# Revit family: Tables-Meeting-Teknion-BC_MRLB_Rectangular_Meeting_Table_Blade_Legs-R2019
name_source: partatom
category: Furniture
units: mm (PartAtom-declared; Revit-internal decimal feet)

## family parameters
Always vertical = Yes
Cut with Voids When Loaded = No
OmniClass Number = 23.40.20.00
OmniClass Title = General Furniture and Specialties
Room Calculation Point = No
Shared = Yes
Work Plane-Based = No

## types (6) — shared parameters
Assembly Code = E2020200
Manufacturer = Teknion
Manufacturer Fax = 416.661.4586
Part Number = BC_MRLB
Product Documentation Link = https://www.teknion.com
Product Line = Expansion Casegoods
Product Page URL = https://www.teknion.com
Series = Expansion Casegoods
Sustainability Data = https://www.teknion.com
URL = www.teknion.com
Unit Weight URL = http://www.teknion.com
Warranty = http://www.teknion.com

## per-type parameters (varying)
| type | Depth | Description | Height | Model | Worksurface Thickness |
| 1" Worksurface Thickness, 42" Depth | 41.79 " | Rectangular Meeting Table - Blade Legs, 1" Worksurface Thickness, 42" Depth | 28.823 " | BCDMRLB42_____ | 1.016 " |
| 1" Worksurface Thickness, 48" Depth | 47.76 " | Rectangular Meeting Table - Blade Legs, 1" Worksurface Thickness, 48" Depth | 28.823 " | BCDMRLB48_____ | 1.016 " |
| 1 3/16" Worksurface Thickness, 42" Depth | 41.79 " | Rectangular Meeting Table - Blade Legs, 1 3/16" Worksurface Thickness, 42" Depth | 28.996 " | BCMMRLB42_____ | 1.189 " |
| 1 3/16" Worksurface Thickness, 48" Depth | 47.76 " | Rectangular Meeting Table - Blade Legs, 1 3/16" Worksurface Thickness, 48" Depth | 28.996 " | BCMMRLB48_____ | 1.189 " |
| 1 9/16" Worksurface Thickness, 48" Depth | 47.76 " | Rectangular Meeting Table - Blade Legs, 1 9/16" Worksurface Thickness, 48" Depth | 29.362 " | BCXMRLB48_____ | 1.555 " |
| 1 9/16" Worksurface Thickness, 42" Depth | 41.79 " | Rectangular Meeting Table - Blade Legs, 1 9/16" Worksurface Thickness, 42" Depth | 29.362 " | BCXMRLB42_____ | 1.555 " |

## geometry (parser evidence)
native form markers: Sweep x5
no freeform markers — native parametric forms only
